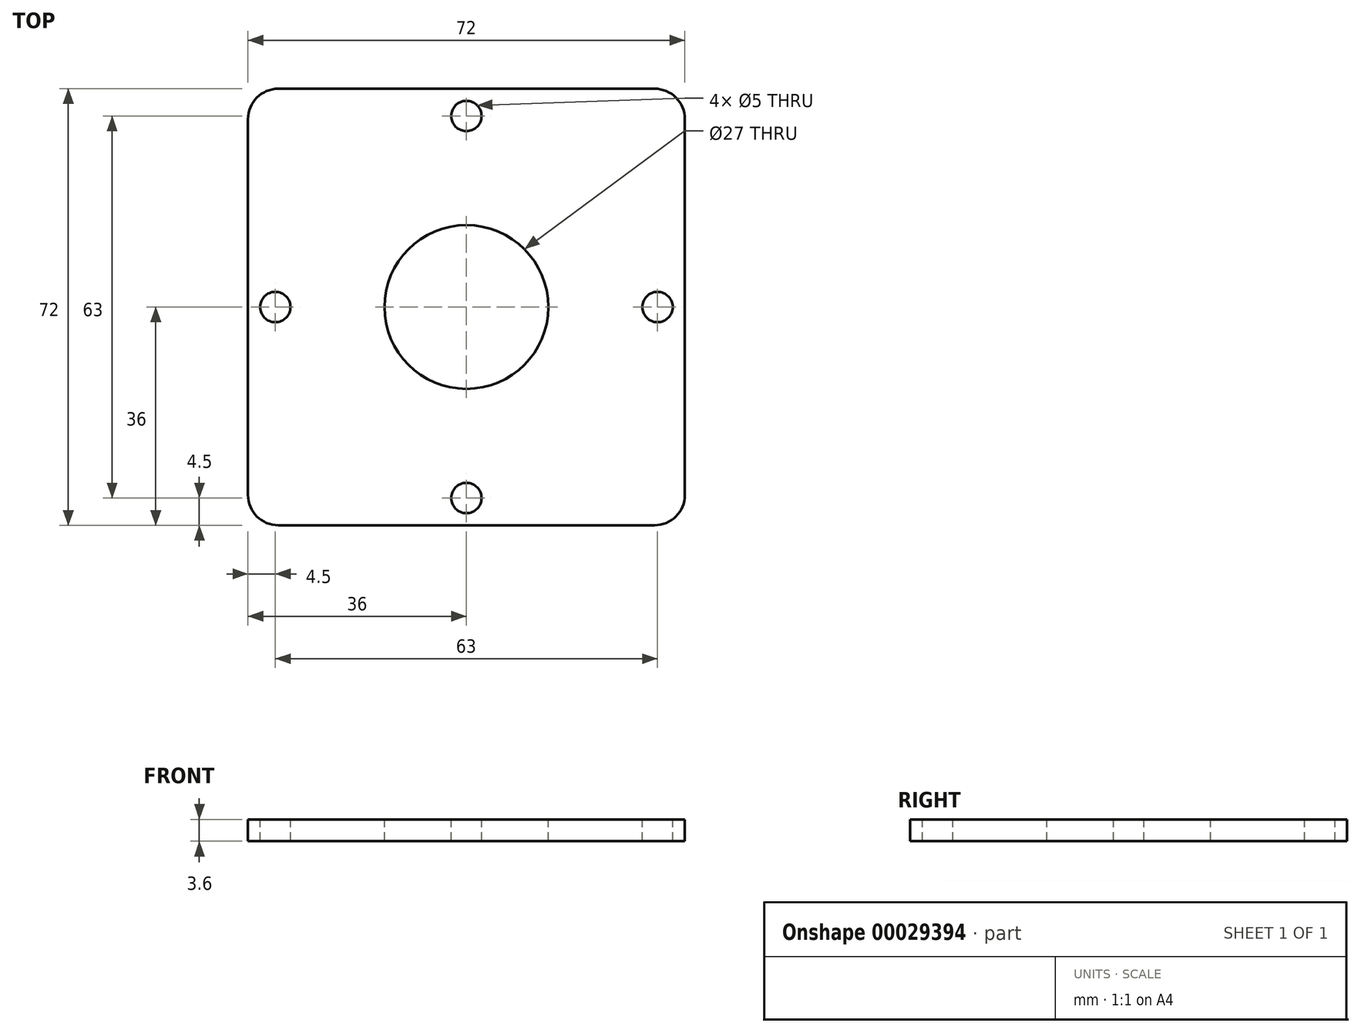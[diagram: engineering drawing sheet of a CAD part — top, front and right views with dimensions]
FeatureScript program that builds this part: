
annotation { "Feature Type Name" : "Feature", "Feature Type Description" : "" }
export const myFeature = defineFeature(function(context is Context, id is Id, definition is map)
    precondition{}
    {
        {
            var Q0;
            Q0=qCreatedBy(makeId("Top.planeOp"),FACE);
            var sketch = newSketch(context, id + "F0", { "sketchPlane" : qUnion([Q0])});
            skLineSegment(sketch, "E0.rect.bottom", {"start": v(36, 36) * mm, "end": v(-36, 36) * mm});
            skLineSegment(sketch, "E0.rect.top", {"start": v(36, -36) * mm, "end": v(-36, -36) * mm});
            skLineSegment(sketch, "E0.rect.left", {"start": v(36, 36) * mm, "end": v(36, -36) * mm});
            skLineSegment(sketch, "E0.rect.right", {"start": v(-36, 36) * mm, "end": v(-36, -36) * mm});
            skPoint(sketch, "E0.rect.middle", {"position": v(0, 0) * mm});
            skSolve(sketch);
        }
        {
            var Q0;
            Q0 = qSketchRegion(id + "F0", true);
            extrude(context, id + "F1", {"entities" : qUnion([Q0]), "depth" : 3.6 * mm});
        }
        {
            var Q0;
            Q0=makeQuery(id+"F1.opExtrude","SWEPT_EDGE",EDGE,{"disambiguationData":[OSD([sQuery(id+"F0.wireOp",EDGE,"E0.rect.top"),sQuery(id+"F0.wireOp",EDGE,"E0.rect.right")])]});
            var Q1;
            Q1=makeQuery(id+"F1.opExtrude","SWEPT_EDGE",EDGE,{"disambiguationData":[OSD([sQuery(id+"F0.wireOp",EDGE,"E0.rect.top"),sQuery(id+"F0.wireOp",EDGE,"E0.rect.left")])]});
            var Q2;
            Q2=makeQuery(id+"F1.opExtrude","SWEPT_EDGE",EDGE,{"disambiguationData":[OSD([sQuery(id+"F0.wireOp",EDGE,"E0.rect.bottom"),sQuery(id+"F0.wireOp",EDGE,"E0.rect.left")])]});
            var Q3;
            Q3=makeQuery(id+"F1.opExtrude","SWEPT_EDGE",EDGE,{"disambiguationData":[OSD([sQuery(id+"F0.wireOp",EDGE,"E0.rect.bottom"),sQuery(id+"F0.wireOp",EDGE,"E0.rect.right")])]});
            fillet(context, id + "F2", {"entities" : qUnion([Q0, Q1, Q2, Q3]), "radius" : 5 * mm, "tangentPropagation" : true, "allowEdgeOverflow" : false});
        }
        {
            var Q0;
            Q0=makeQuery(id+"F1.opExtrude","CAP_FACE",FACE,{"disambiguationData":[OSD([sQuery(id+"F0.wireOp",EDGE,"E0.rect.bottom"),sQuery(id+"F0.wireOp",EDGE,"E0.rect.top"),sQuery(id+"F0.wireOp",EDGE,"E0.rect.left"),sQuery(id+"F0.wireOp",EDGE,"E0.rect.right")])],"isStart":false});
            var sketch = newSketch(context, id + "F3", { "sketchPlane" : qUnion([Q0])});
            skCircle(sketch, "E1", {"center": v(0, 0) * mm, "radius": 13.5 * mm});
            skSolve(sketch);
        }
        {
            var Q0;
            Q0 = qSketchRegion(id + "F3", true);
            extrude(context, id + "F4", {"entities" : qUnion([Q0]), "operationType" : NewBodyOperationType.REMOVE, "oppositeDirection" : true, "depth" : 3.6 * mm});
        }
        {
            var Q0;
            Q0=makeQuery(id+"F1.opExtrude","CAP_FACE",FACE,{"disambiguationData":[OSD([sQuery(id+"F0.wireOp",EDGE,"E0.rect.bottom"),sQuery(id+"F0.wireOp",EDGE,"E0.rect.top"),sQuery(id+"F0.wireOp",EDGE,"E0.rect.left"),sQuery(id+"F0.wireOp",EDGE,"E0.rect.right")])],"isStart":false});
            var sketch = newSketch(context, id + "F5", { "sketchPlane" : qUnion([Q0])});
            skLineSegment(sketch, "E2", {"start": v(0, 0) * mm, "end": v(0, 36) * mm, "construction": true});
            skLineSegment(sketch, "E3", {"start": v(0, 0) * mm, "end": v(0, -36) * mm, "construction": true});
            skLineSegment(sketch, "E4", {"start": v(0, 0) * mm, "end": v(-36, 0) * mm, "construction": true});
            skLineSegment(sketch, "E5", {"start": v(0, 0) * mm, "end": v(36, 0) * mm, "construction": true});
            skCircle(sketch, "E6", {"center": v(0, 31.5) * mm, "radius": 2.5 * mm});
            skCircle(sketch, "E7", {"center": v(-31.5, 0) * mm, "radius": 2.5 * mm});
            skCircle(sketch, "E8", {"center": v(0, -31.5) * mm, "radius": 2.5 * mm});
            skCircle(sketch, "E9", {"center": v(31.5, 0) * mm, "radius": 2.5 * mm});
            skSolve(sketch);
        }
        {
            var Q0;
            Q0 = qSketchRegion(id + "F5", true);
            extrude(context, id + "F6", {"entities" : qUnion([Q0]), "operationType" : NewBodyOperationType.REMOVE, "oppositeDirection" : true, "depth" : 3.6 * mm});
        }
    });
